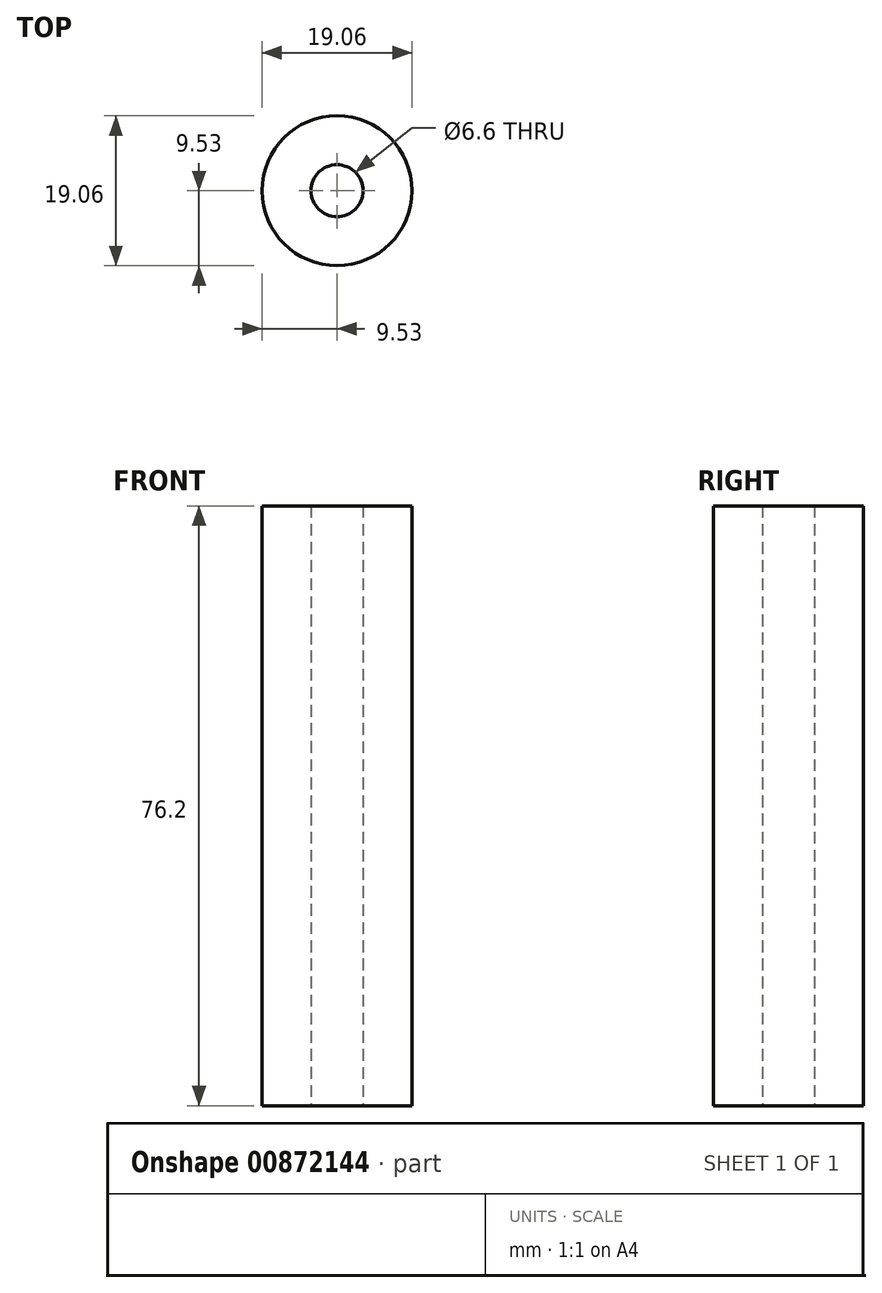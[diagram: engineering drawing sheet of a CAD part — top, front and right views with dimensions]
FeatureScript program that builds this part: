
annotation { "Feature Type Name" : "Feature", "Feature Type Description" : "" }
export const myFeature = defineFeature(function(context is Context, id is Id, definition is map)
    precondition{}
    {
        {
            var Q0;
            Q0=qCreatedBy(makeId("Top.planeOp"),FACE);
            var sketch = newSketch(context, id + "F0", { "sketchPlane" : qUnion([Q0])});
            skCircle(sketch, "E0", {"center": v(0, 0) * mm, "radius": 9.53 * mm});
            skCircle(sketch, "E1", {"center": v(0, 0) * mm, "radius": 3.3 * mm});
            skSolve(sketch);
        }
        {
            var Q0;
            Q0 = qSketchRegion(id + "F0", true);
            extrude(context, id + "F1", {"entities" : qUnion([Q0]), "depth" : 76.2 * mm, "offsetDistance" : 25.4 * mm});
        }
    });
